# Revit family: C_CCS50_2DO_CAD_MULT_Prod
name_source: partatom
category: Detail Items
revit_build: Autodesk Revit 2015 (Build: 20140606_1530(x64)
units: mm (PartAtom-declared; Revit-internal decimal feet)

## types (4) — shared parameters
Density = 0.26 kg
Description = Connector Other
EPD = https://www.strongtie.eu
ETA / DoP = https://www.strongtie.eu
Manufacturer = Simpson Strong-Tie
Model = CCS50
Model Disclaimer = Contact Simpson Strong-Tie Company  for more information
Model ID = 0201323967302532185531204864958884444244
Name = CCS50
ObjectType = CCS50
Product Material = ElectroGalvanised
Product Type = Connector Other
Reference = CCS50
Technical datasheet = https://www.strongtie.eu
URL = www.strongtie.eu
UniClass Number = Pr_20_85_09_52
UniClass Title = Metal timber member fixing brackets

## per-type parameters (varying)
| type | _visiblefront | _visibleleft | _visibleright | _visibletop |
| SST_CCS50_Front | Yes | No | No | No |
| SST_CCS50_Top | No | No | No | Yes |
| SST_CCS50_Left | No | Yes | No | No |
| SST_CCS50_Right | No | No | Yes | No |

## geometry (parser evidence)
native form markers: Sweep x2
no freeform markers — native parametric forms only
